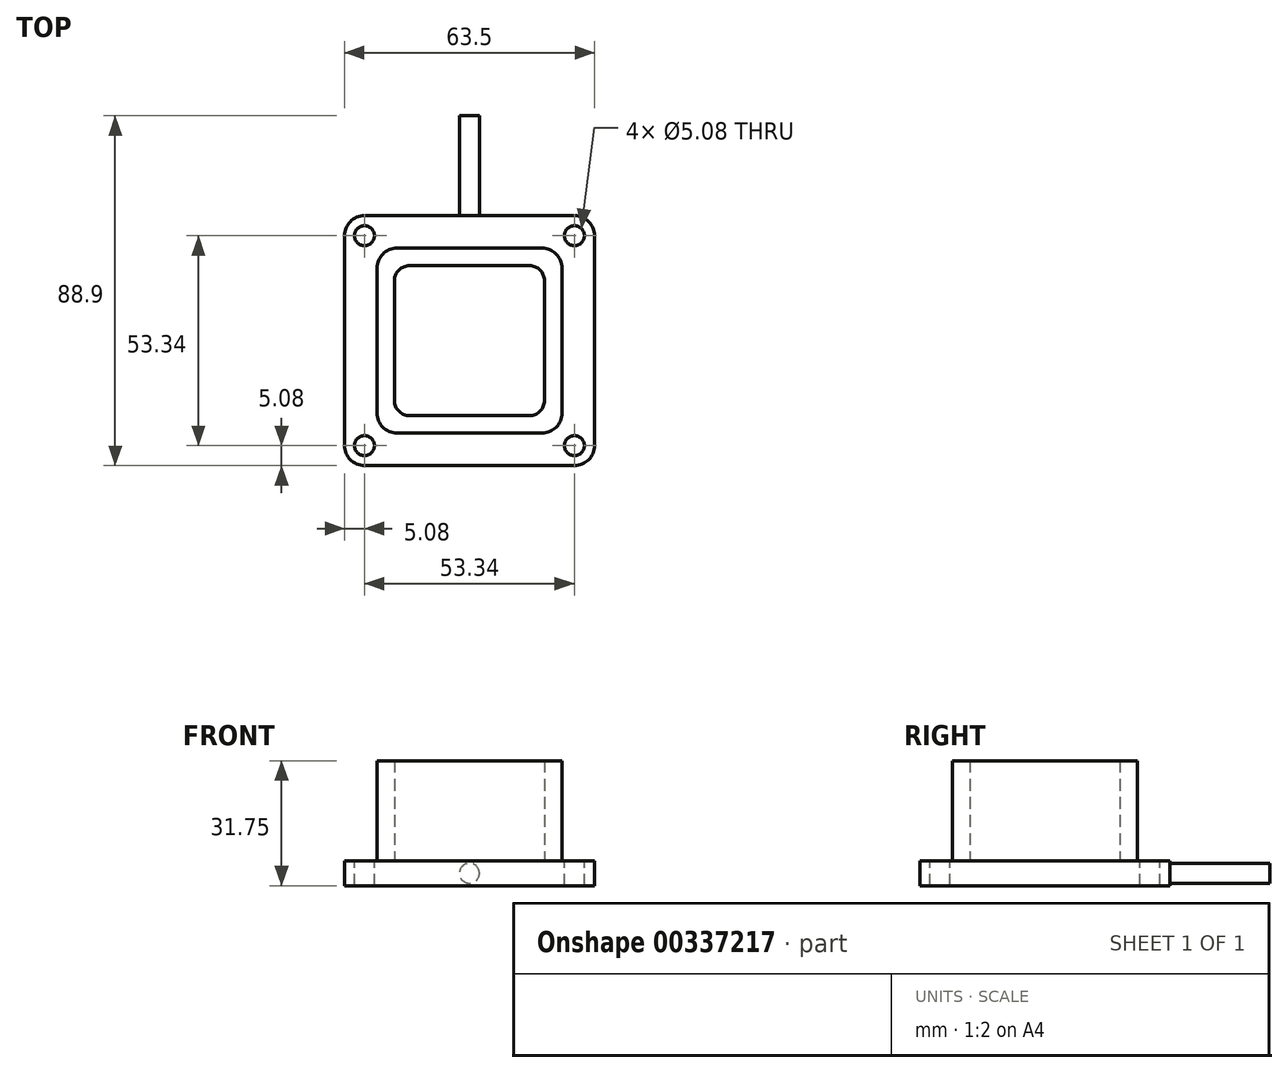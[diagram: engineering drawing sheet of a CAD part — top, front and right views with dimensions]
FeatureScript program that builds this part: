
annotation { "Feature Type Name" : "Feature", "Feature Type Description" : "" }
export const myFeature = defineFeature(function(context is Context, id is Id, definition is map)
    precondition{}
    {
        {
            var Q0;
            Q0=qCreatedBy(makeId("Top.planeOp"),FACE);
            var sketch = newSketch(context, id + "F0", { "sketchPlane" : qUnion([Q0])});
            skLineSegment(sketch, "E0.bottom", {"start": v(31.75, -31.75) * mm, "end": v(-31.75, -31.75) * mm});
            skLineSegment(sketch, "E0.top", {"start": v(31.75, 31.75) * mm, "end": v(-31.75, 31.75) * mm});
            skLineSegment(sketch, "E0.left", {"start": v(31.75, -31.75) * mm, "end": v(31.75, 31.75) * mm});
            skLineSegment(sketch, "E0.right", {"start": v(-31.75, -31.75) * mm, "end": v(-31.75, 31.75) * mm});
            skPoint(sketch, "E0.middle", {"position": v(0, 0) * mm});
            skSolve(sketch);
        }
        {
            var Q0;
            Q0=makeQuery(id+"F0.imprint","IMPRINT",FACE,{"disambiguationData":[TD([[makeQuery(id+"F0.imprint","IMPRINT",EDGE,{"derivedFrom":sQuery(id+"F0.wireOp",EDGE,"E0.bottom")}),-1.0]])]});
            extrude(context, id + "F1", {"entities" : qUnion([Q0]), "depth" : 6.35 * mm});
        }
        {
            var Q0;
            Q0=makeQuery(id+"F1.opExtrude","SWEPT_EDGE",EDGE,{"disambiguationData":[OSD([sQuery(id+"F0.wireOp",EDGE,"E0.bottom"),sQuery(id+"F0.wireOp",EDGE,"E0.right")])]});
            var Q1;
            Q1=makeQuery(id+"F1.opExtrude","SWEPT_EDGE",EDGE,{"disambiguationData":[OSD([sQuery(id+"F0.wireOp",EDGE,"E0.bottom"),sQuery(id+"F0.wireOp",EDGE,"E0.left")])]});
            var Q2;
            Q2=makeQuery(id+"F1.opExtrude","SWEPT_EDGE",EDGE,{"disambiguationData":[OSD([sQuery(id+"F0.wireOp",EDGE,"E0.top"),sQuery(id+"F0.wireOp",EDGE,"E0.left")])]});
            var Q3;
            Q3=makeQuery(id+"F1.opExtrude","SWEPT_EDGE",EDGE,{"disambiguationData":[OSD([sQuery(id+"F0.wireOp",EDGE,"E0.top"),sQuery(id+"F0.wireOp",EDGE,"E0.right")])]});
            fillet(context, id + "F2", {"entities" : qUnion([Q0, Q1, Q2, Q3]), "radius" : 5.08 * mm, "tangentPropagation" : true, "allowEdgeOverflow" : false});
        }
        {
            var Q0;
            Q0=makeQuery(id+"F1.opExtrude","CAP_FACE",FACE,{"disambiguationData":[OSD([sQuery(id+"F0.wireOp",EDGE,"E0.bottom"),sQuery(id+"F0.wireOp",EDGE,"E0.top"),sQuery(id+"F0.wireOp",EDGE,"E0.left"),sQuery(id+"F0.wireOp",EDGE,"E0.right")])],"isStart":false});
            var sketch = newSketch(context, id + "F3", { "sketchPlane" : qUnion([Q0])});
            skLineSegment(sketch, "E1.bottom", {"start": v(-26.67, 26.67) * mm, "end": v(26.67, 26.67) * mm});
            skLineSegment(sketch, "E1.top", {"start": v(-26.67, -26.67) * mm, "end": v(26.67, -26.67) * mm});
            skLineSegment(sketch, "E1.left", {"start": v(-26.67, 26.67) * mm, "end": v(-26.67, -26.67) * mm});
            skLineSegment(sketch, "E1.right", {"start": v(26.67, 26.67) * mm, "end": v(26.67, -26.67) * mm});
            skPoint(sketch, "E1.middle", {"position": v(0, 0) * mm});
            skSolve(sketch);
        }
        {
            var Q0;
            Q0=sQuery(id+"F3.wireOp",VERTEX,"E1.bottom.start");
            var Q1;
            Q1=sQuery(id+"F3.wireOp",VERTEX,"E1.right.start");
            var Q2;
            Q2=sQuery(id+"F3.wireOp",VERTEX,"E1.right.end");
            var Q3;
            Q3=sQuery(id+"F3.wireOp",VERTEX,"E1.left.end");
            var Q4;
            Q4=makeQuery(id+"F1.opExtrude","SWEPT_BODY",BODY,{"disambiguationData":[OSD([sQuery(id+"F0.wireOp",EDGE,"E0.bottom"),sQuery(id+"F0.wireOp",EDGE,"E0.top"),sQuery(id+"F0.wireOp",EDGE,"E0.left"),sQuery(id+"F0.wireOp",EDGE,"E0.right")])]});
            hole(context, id + "F4", {"style" : HoleStyle.SIMPLE, "endStyle" : HoleEndStyle.THROUGH, "holeDiameter" : 5.08 * mm, "tappedDepth" : 12.7 * mm, "tapClearance" : 3, "locations" : qUnion([Q0, Q1, Q2, Q3]), "scope" : qUnion([Q4])});
        }
        {
            var Q0;
            Q0=makeQuery(id+"F1.opExtrude","SWEPT_FACE",FACE,{"disambiguationData":[OSD([sQuery(id+"F0.wireOp",EDGE,"E0.top")])]});
            var sketch = newSketch(context, id + "F5", { "sketchPlane" : qUnion([Q0])});
            skCircle(sketch, "E2", {"center": v(0, 3.18) * mm, "radius": 2.54 * mm});
            skPoint(sketch, "E2.centerSnap0", {"position": v(-26.67, 3.18) * mm});
            skPoint(sketch, "E2.centerSnap1", {"position": v(0, 0) * mm});
            skSolve(sketch);
        }
        {
            var Q0;
            Q0=makeQuery(id+"F5.imprint","IMPRINT",FACE,{"disambiguationData":[TD([[makeQuery(id+"F5.imprint","IMPRINT",EDGE,{"derivedFrom":sQuery(id+"F5.wireOp",EDGE,"E2")}),1.0]])]});
            extrude(context, id + "F6", {"entities" : qUnion([Q0]), "operationType" : NewBodyOperationType.ADD, "depth" : 25.4 * mm});
        }
        {
            var Q0;
            Q0=makeQuery(id+"F1.opExtrude","CAP_FACE",FACE,{"disambiguationData":[OSD([sQuery(id+"F0.wireOp",EDGE,"E0.bottom"),sQuery(id+"F0.wireOp",EDGE,"E0.top"),sQuery(id+"F0.wireOp",EDGE,"E0.left"),sQuery(id+"F0.wireOp",EDGE,"E0.right")])],"isStart":false});
            var sketch = newSketch(context, id + "F7", { "sketchPlane" : qUnion([Q0])});
            skLineSegment(sketch, "E3.bottom", {"start": v(-19.05, 19.05) * mm, "end": v(19.05, 19.05) * mm});
            skLineSegment(sketch, "E3.top", {"start": v(-19.05, -19.05) * mm, "end": v(19.05, -19.05) * mm});
            skLineSegment(sketch, "E3.left", {"start": v(-19.05, 19.05) * mm, "end": v(-19.05, -19.05) * mm});
            skLineSegment(sketch, "E3.right", {"start": v(19.05, 19.05) * mm, "end": v(19.05, -19.05) * mm});
            skPoint(sketch, "E3.middle", {"position": v(0, 0) * mm});
            skLineSegment(sketch, "E4.bottom", {"start": v(-23.5, 23.5) * mm, "end": v(23.5, 23.5) * mm});
            skLineSegment(sketch, "E4.top", {"start": v(-23.5, -23.5) * mm, "end": v(23.5, -23.5) * mm});
            skLineSegment(sketch, "E4.left", {"start": v(-23.5, 23.5) * mm, "end": v(-23.5, -23.5) * mm});
            skLineSegment(sketch, "E4.right", {"start": v(23.5, 23.5) * mm, "end": v(23.5, -23.5) * mm});
            skSolve(sketch);
        }
        {
            var Q0;
            Q0=makeQuery(id+"F7.imprint","IMPRINT",FACE,{"disambiguationData":[TD([[makeQuery(id+"F7.imprint","IMPRINT",EDGE,{"derivedFrom":sQuery(id+"F7.wireOp",EDGE,"E3.bottom")}),1.0]])]});
            extrude(context, id + "F8", {"entities" : qUnion([Q0]), "operationType" : NewBodyOperationType.ADD, "depth" : 25.4 * mm});
        }
        {
            var Q0;
            Q0=makeQuery(id+"F8.opExtrude","SWEPT_EDGE",EDGE,{"disambiguationData":[OSD([sQuery(id+"F7.wireOp",EDGE,"E4.top"),sQuery(id+"F7.wireOp",EDGE,"E4.left")])]});
            var Q1;
            Q1=makeQuery(id+"F8.opExtrude","SWEPT_EDGE",EDGE,{"disambiguationData":[OSD([sQuery(id+"F7.wireOp",EDGE,"E4.top"),sQuery(id+"F7.wireOp",EDGE,"E4.right")])]});
            var Q2;
            Q2=makeQuery(id+"F8.opExtrude","SWEPT_EDGE",EDGE,{"disambiguationData":[OSD([sQuery(id+"F7.wireOp",EDGE,"E4.bottom"),sQuery(id+"F7.wireOp",EDGE,"E4.right")])]});
            var Q3;
            Q3=makeQuery(id+"F8.opExtrude","SWEPT_EDGE",EDGE,{"disambiguationData":[OSD([sQuery(id+"F7.wireOp",EDGE,"E4.bottom"),sQuery(id+"F7.wireOp",EDGE,"E4.left")])]});
            fillet(context, id + "F9", {"entities" : qUnion([Q0, Q1, Q2, Q3]), "radius" : 5.08 * mm, "tangentPropagation" : true, "allowEdgeOverflow" : false});
        }
        {
            var Q0;
            Q0=makeQuery(id+"F8.opExtrude","SWEPT_EDGE",EDGE,{"disambiguationData":[OSD([sQuery(id+"F7.wireOp",EDGE,"E3.bottom"),sQuery(id+"F7.wireOp",EDGE,"E3.right")])]});
            var Q1;
            Q1=makeQuery(id+"F8.opExtrude","SWEPT_EDGE",EDGE,{"disambiguationData":[OSD([sQuery(id+"F7.wireOp",EDGE,"E3.bottom"),sQuery(id+"F7.wireOp",EDGE,"E3.left")])]});
            var Q2;
            Q2=makeQuery(id+"F8.opExtrude","SWEPT_EDGE",EDGE,{"disambiguationData":[OSD([sQuery(id+"F7.wireOp",EDGE,"E3.top"),sQuery(id+"F7.wireOp",EDGE,"E3.left")])]});
            var Q3;
            Q3=makeQuery(id+"F8.opExtrude","SWEPT_EDGE",EDGE,{"disambiguationData":[OSD([sQuery(id+"F7.wireOp",EDGE,"E3.top"),sQuery(id+"F7.wireOp",EDGE,"E3.right")])]});
            fillet(context, id + "F10", {"entities" : qUnion([Q0, Q1, Q2, Q3]), "radius" : 3.8 * mm, "tangentPropagation" : true, "allowEdgeOverflow" : false});
        }
    });
